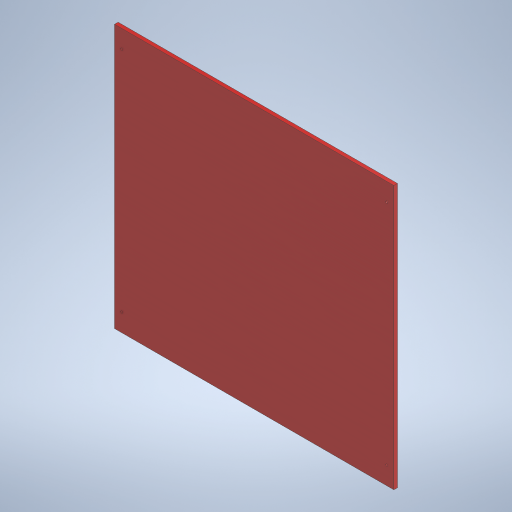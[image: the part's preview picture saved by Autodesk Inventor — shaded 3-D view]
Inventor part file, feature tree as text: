
AUTODESK INVENTOR PART (.ipt)
format: ipt  version: 2023.2 (Build 272271030, 271C)  size: 238,080 bytes
history: native  units: mm
features: extrude x1, sketch x1
ambient origin geometry x8: Origin, YZ Plane, XZ Plane, XY Plane, X Axis, Y Axis, Z Axis, Center Point
bodies: Solid1 (feature_tree)
feature tree (2):
  extrude  "Extrusion1"  Depth=780.0mm
  sketch  "Sketch1"  dims[d0=736.0mm d1=780.0mm d2=5.1mm d3=317.8995mm d4=740.0mm d5=10.0mm d6=0.0mm]
